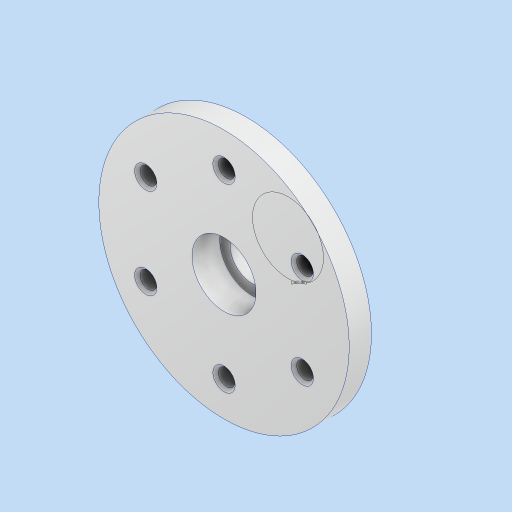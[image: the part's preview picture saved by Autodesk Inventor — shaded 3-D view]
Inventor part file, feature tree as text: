
AUTODESK INVENTOR PART (.ipt)
format: ipt  version: 2023 (Build 270158000, 158)  size: 231,424 bytes
history: native  units: in
note: dims shown in document units (in); Inventor stores cm internally (conversion verified against a paired STEP export)
features: sketch x4, plane x2, extrude x2, hole x2, other x2, chamfer x1, pattern_circular x1, projected_geometry x1
ambient origin geometry x8: Origin, YZ Plane, XZ Plane, XY Plane, X Axis, Y Axis, Z Axis, Center Point
bodies: Solid1 (feature_tree)
feature tree (15):
  plane  "Work Plane1"
  sketch  "Sketch1"  dims[d0=1.375in d1=2.5591in]
  extrude  "Extrusion1"  Depth=2.5591in
  plane  "Work Plane2"
  extrude  "Extrusion2"  Depth=0.2362in
  hole  "Hole1"  [1 undecoded]
  chamfer  "Chamfer1"  Distance=0.5906in
  hole  "Hole2"  [1 undecoded]
  pattern_circular  "Circular Pattern1"  [2 undecoded]
  sketch  "Sketch6"  dims[d20=0.6102in d21=0.2362in d22=0.9055in d23=0.3937in d24=90.0deg d25=0.315in d26=0.8108in d27=0.0394in d28=0.0787in d29=45.0deg d30=0.2559in d31=0.2362in d32=0.2756in d33=0.0787in d34=90.0deg d35=0.2362in d36=0.0in d37=1.0039in d38=1.9685in d39=360.0deg d41=1.9685in d43=360.0deg]
  sketch  "Sketch4"  dims[d2=3.5433in d3=0.2362in]
  sketch  "Sketch5"  dims[d4=2.3622in d6=360.0deg d8=0.315in d9=0.0in d10=0.5906in d11=0.0in]
  projected_geometry  "Projected Loop1"
  other  "Assembly1"
  other  "177x35x10 bearing:1"
note: 4 required parameter values undecoded (feature->parameter linkage not recoverable at this tier; creation-order binding heuristic only, values carry confidence <= 0.55)
